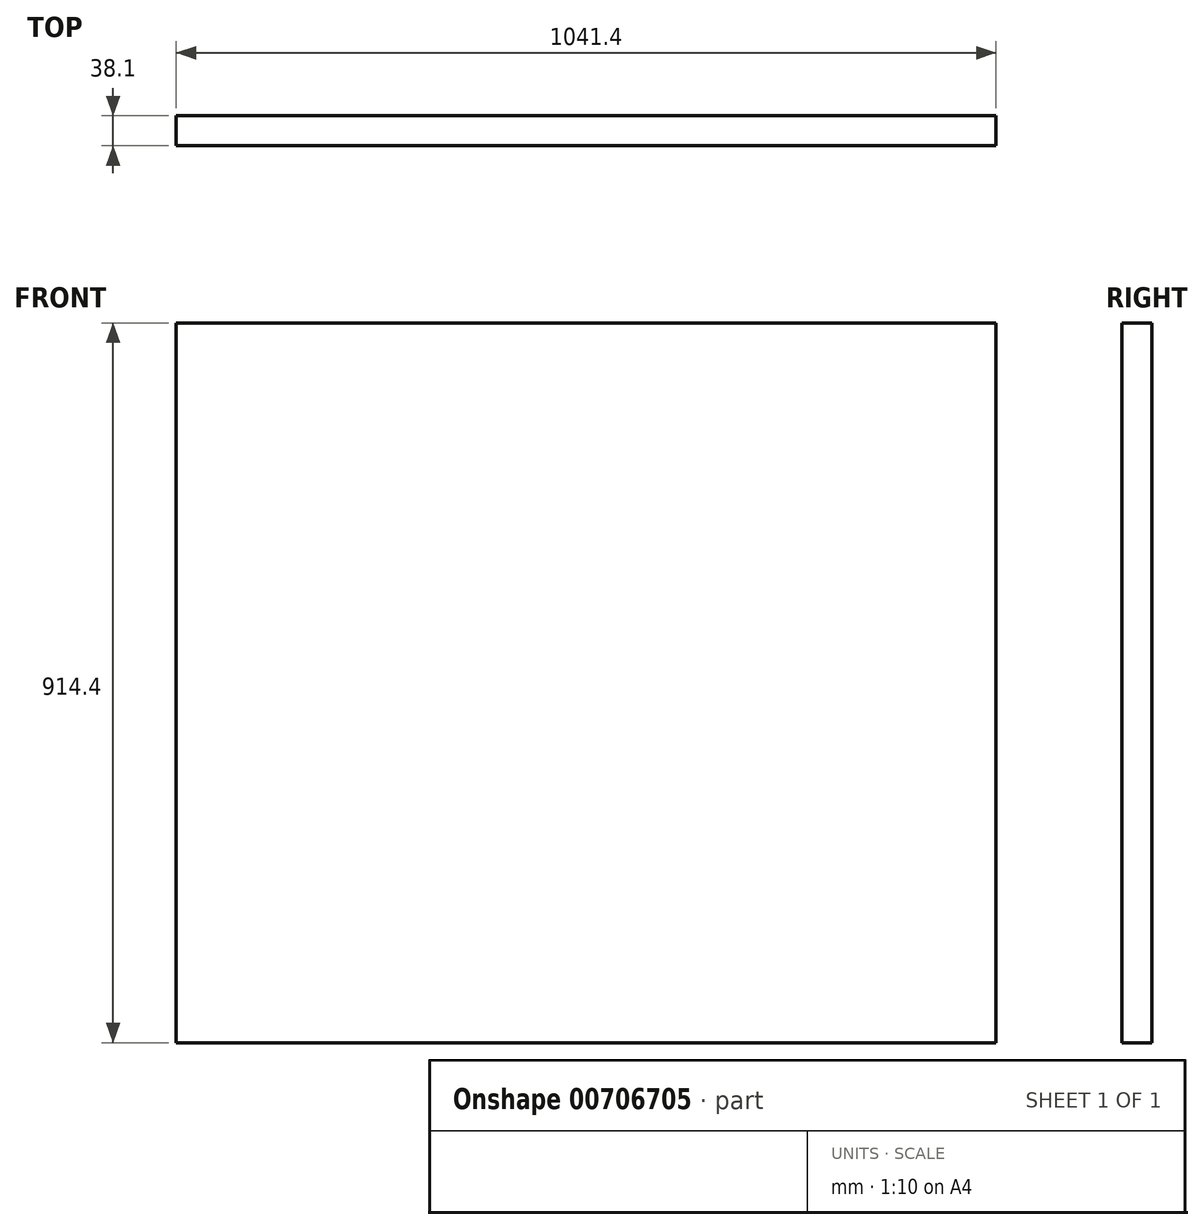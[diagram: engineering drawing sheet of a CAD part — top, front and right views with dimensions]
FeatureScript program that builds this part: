
annotation { "Feature Type Name" : "Feature", "Feature Type Description" : "" }
export const myFeature = defineFeature(function(context is Context, id is Id, definition is map)
    precondition{}
    {
        {
            var Q0;
            Q0=qCreatedBy(makeId("Front.planeOp"),FACE);
            var sketch = newSketch(context, id + "F0", { "sketchPlane" : qUnion([Q0])});
            skLineSegment(sketch, "E0.bottom", {"start": v(0, 0) * mm, "end": v(1041.4, 0) * mm});
            skLineSegment(sketch, "E0.top", {"start": v(0, 914.4) * mm, "end": v(1041.4, 914.4) * mm});
            skLineSegment(sketch, "E0.left", {"start": v(0, 0) * mm, "end": v(0, 914.4) * mm});
            skLineSegment(sketch, "E0.right", {"start": v(1041.4, 0) * mm, "end": v(1041.4, 914.4) * mm});
            skSolve(sketch);
        }
        {
            var Q0;
            Q0=makeQuery(id+"F0.imprint","IMPRINT",FACE,{"disambiguationData":[TD([[makeQuery(id+"F0.imprint","IMPRINT",EDGE,{"derivedFrom":sQuery(id+"F0.wireOp",EDGE,"E0.bottom")}),1.0]])]});
            extrude(context, id + "F1", {"entities" : qUnion([Q0]), "depth" : 38.1 * mm, "offsetDistance" : 25.4 * mm});
        }
    });
